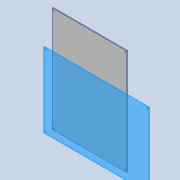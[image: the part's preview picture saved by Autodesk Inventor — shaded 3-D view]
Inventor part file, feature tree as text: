
AUTODESK INVENTOR PART (.ipt)
format: ipt  version: 2020 (Build 240168000, 168)  size: 98,816 bytes
history: native  units: mm
features: sketch x2, extrude x1, hole x1
ambient origin geometry x8: Origin, YZ Plane, XZ Plane, XY Plane, X Axis, Y Axis, Z Axis, Center Point
bodies: Solid1 (feature_tree)
feature tree (4):
  extrude  "Extrusion1"  Depth=325.0mm
  hole  "Hole1"  [1 undecoded]
  sketch  "Sketch1"  dims[d0=230.0mm d1=325.0mm]
  sketch  "Sketch2"  dims[d2=3.0mm d3=0.0mm d4=5.0mm d5=5.0mm d6=3.5mm d7=6.0mm d8=4.0mm d9=2.0mm d10=90.0deg d11=21.0mm d12=0.0mm]
note: 1 required parameter value undecoded (feature->parameter linkage not recoverable at this tier; creation-order binding heuristic only, values carry confidence <= 0.55)
